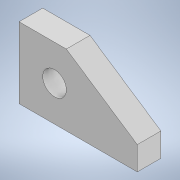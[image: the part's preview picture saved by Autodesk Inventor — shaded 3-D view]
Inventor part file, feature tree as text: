
AUTODESK INVENTOR PART (.ipt)
format: ipt  version: 2022 (Build 260153000, 153)  size: 98,816 bytes
history: native  units: mm
features: other x1, extrude x1, sketch x1
ambient origin geometry x8: Origin, YZ Plane, XZ Plane, XY Plane, X Axis, Y Axis, Z Axis, Center Point
bodies: Body1 (feature_tree)
feature tree (3):
  other  "Sólido1"
  extrude  "Extrusão1"  Depth=10.0mm
  sketch  "Esboço1"  dims[d0=50.0mm d1=10.0mm d2=30.0mm d3=20.0mm d4=10.0mm d5=15.0mm d6=15.0mm d7=10.0mm d8=0.0mm]
